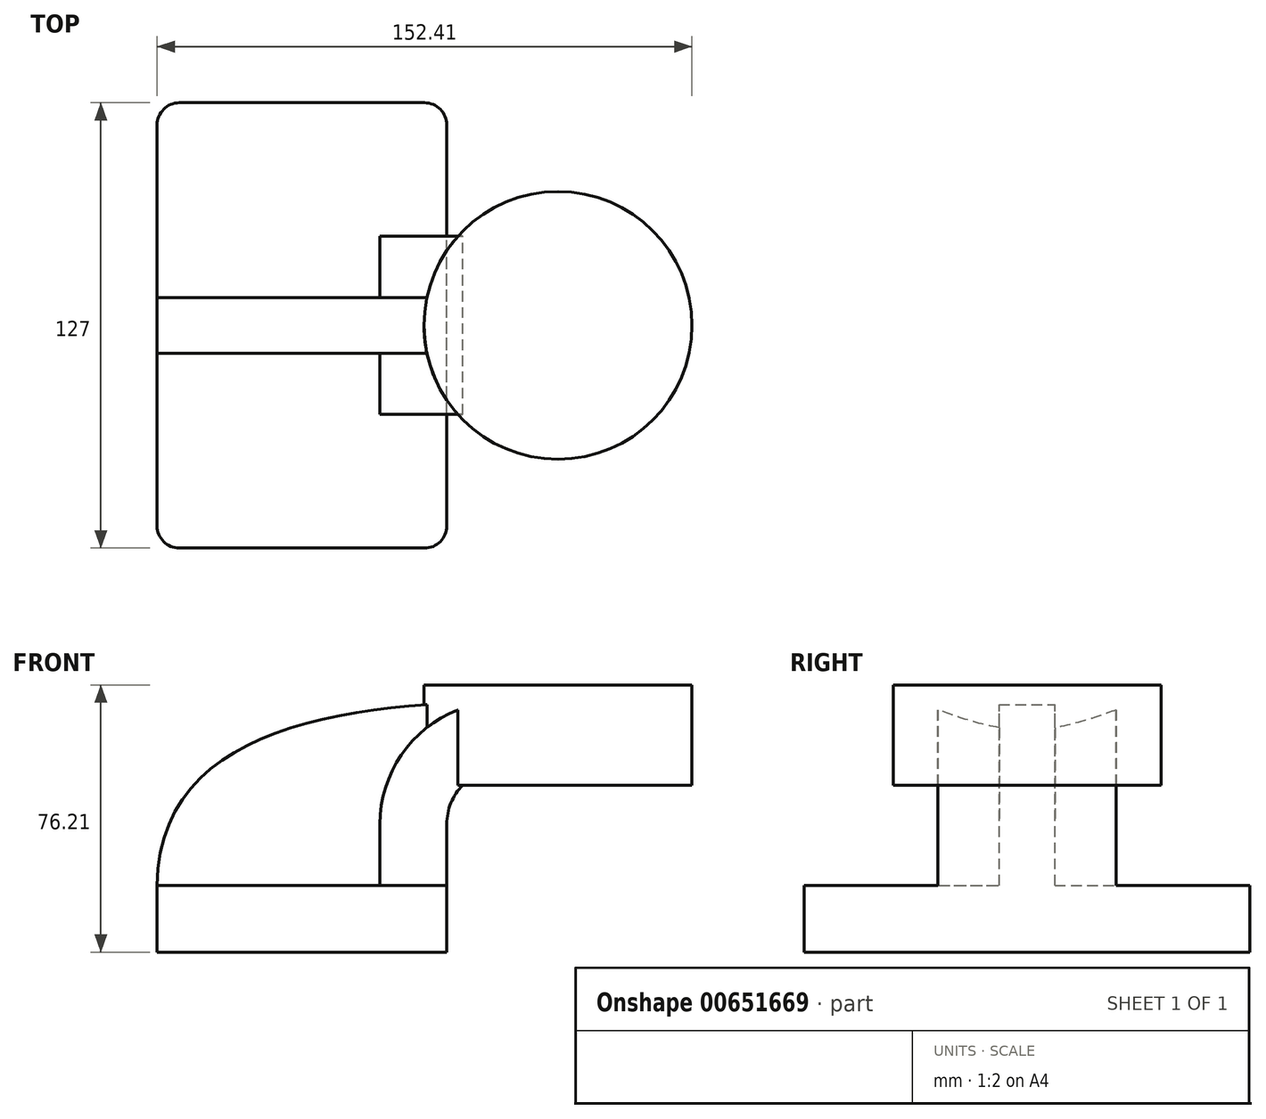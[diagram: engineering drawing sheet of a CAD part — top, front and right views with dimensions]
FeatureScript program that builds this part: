
annotation { "Feature Type Name" : "Feature", "Feature Type Description" : "" }
export const myFeature = defineFeature(function(context is Context, id is Id, definition is map)
    precondition{}
    {
        {
            var Q0;
            Q0=qCreatedBy(makeId("Front.planeOp"),FACE);
            var sketch = newSketch(context, id + "F0", { "sketchPlane" : qUnion([Q0])});
            skLineSegment(sketch, "E0.bottom", {"start": v(-41.28, 9.52) * mm, "end": v(41.27, 9.53) * mm});
            skLineSegment(sketch, "E0.top", {"start": v(-41.28, -9.52) * mm, "end": v(41.28, -9.52) * mm});
            skLineSegment(sketch, "E0.left", {"start": v(-41.28, 9.52) * mm, "end": v(-41.28, -9.53) * mm});
            skLineSegment(sketch, "E0.right", {"start": v(41.27, 9.53) * mm, "end": v(41.28, -9.52) * mm});
            skPoint(sketch, "E0.middle", {"position": v(0, 0) * mm});
            skLineSegment(sketch, "E1.bottom", {"start": v(111.12, 38.1) * mm, "end": v(60.32, 38.1) * mm});
            skLineSegment(sketch, "E1.top", {"start": v(111.12, 66.68) * mm, "end": v(60.32, 66.68) * mm});
            skLineSegment(sketch, "E1.left", {"start": v(111.12, 38.1) * mm, "end": v(111.12, 66.68) * mm});
            skLineSegment(sketch, "E1.right", {"start": v(60.32, 38.1) * mm, "end": v(60.32, 66.68) * mm});
            skPoint(sketch, "E1.middle", {"position": v(85.72, 52.39) * mm});
            skLineSegment(sketch, "E2", {"start": v(41.27, 9.53) * mm, "end": v(41.27, 27) * mm});
            skArc(sketch, "E3", {"start": v(41.27, 27) * mm, "mid": v(45.92, 38.23) * mm, "end": v(57.15, 42.88) * mm});
            skLineSegment(sketch, "E4", {"start": v(57.15, 42.88) * mm, "end": v(72.95, 42.88) * mm});
            skLineSegment(sketch, "E5.0", {"start": v(57.15, 61.93) * mm, "end": v(72.95, 61.93) * mm});
            skArc(sketch, "E5.1", {"start": v(22.22, 27) * mm, "mid": v(32.45, 51.7) * mm, "end": v(57.15, 61.93) * mm});
            skLineSegment(sketch, "E5.2", {"start": v(22.22, 9.53) * mm, "end": v(22.22, 27) * mm});
            skLineSegment(sketch, "E6", {"start": v(72.95, 42.88) * mm, "end": v(72.95, 66.68) * mm});
            skLineSegment(sketch, "E7", {"start": v(72.95, 66.68) * mm, "end": v(72.95, 38.1) * mm});
            skFitSpline(sketch, "E8", {"points": [v(-41.28, 9.52) * mm, v(57.15, 61.93) * mm], "startDerivative": vector(1.24, 134.3) * mm, "endDerivative": vector(138.83, 2.17) * mm});
            skSolve(sketch);
        }
        {
            var Q0;
            Q0=makeQuery(id+"F0.imprint","IMPRINT",FACE,{"disambiguationData":[TD([[makeQuery(id+"F0.imprint","IMPRINT",EDGE,{"derivedFrom":sQuery(id+"F0.wireOp",EDGE,"E0.top")}),1.0]])]});
            extrude(context, id + "F1", {"entities" : qUnion([Q0]), "endBound" : BoundingType.SYMMETRIC, "depth" : 127 * mm, "offsetDistance" : 25.4 * mm});
        }
        {
            var Q0;
            {var subQ1=sQuery(id+"F0.wireOp",EDGE,"E2");Q0=makeQuery(id+"F0.imprint","IMPRINT",FACE,{"disambiguationData":[TD([[makeQuery(id+"F0.imprint","IMPRINT",EDGE,{"derivedFrom":subQ1}),1.0]])]});}
            var Q1;
            {var subQ0=sQuery(id+"F0.wireOp",EDGE,"E4");var subQ1=sQuery(id+"F0.wireOp",EDGE,"E1.right");var subQ2=makeQuery(id+"F0.imprint","INTERSECT",VERTEX,{"derivedFrom":[subQ1,subQ0]});Q1=makeQuery(id+"F0.imprint","IMPRINT",FACE,{"disambiguationData":[TD([[makeQuery(id+"F0.imprint","IMPRINT",EDGE,{"disambiguationData":[TD([[subQ2,-1.0]])],"derivedFrom":subQ1}),-1.0]])]});}
            extrude(context, id + "F2", {"entities" : qUnion([Q0, Q1]), "operationType" : NewBodyOperationType.ADD, "endBound" : BoundingType.SYMMETRIC, "depth" : 50.8 * mm, "offsetDistance" : 25.4 * mm});
        }
        {
            var Q0;
            {var subQ3=sQuery(id+"F0.wireOp",EDGE,"E5.2");Q0=makeQuery(id+"F0.imprint","IMPRINT",FACE,{"disambiguationData":[TD([[makeQuery(id+"F0.imprint","IMPRINT",EDGE,{"derivedFrom":subQ3}),1.0]])]});}
            extrude(context, id + "F3", {"entities" : qUnion([Q0]), "operationType" : NewBodyOperationType.ADD, "endBound" : BoundingType.SYMMETRIC, "depth" : 15.88 * mm, "offsetDistance" : 25.4 * mm});
        }
        {
            var Q0;
            {var subQ0=sQuery(id+"F0.wireOp",EDGE,"E1.left");Q0=makeQuery(id+"F0.imprint","IMPRINT",FACE,{"disambiguationData":[TD([[makeQuery(id+"F0.imprint","IMPRINT",EDGE,{"derivedFrom":subQ0}),1.0]])]});}
            var Q1;
            Q1=sQuery(id+"F0.wireOp",EDGE,"E7");
            revolve(context, id + "F4", {"operationType" : NewBodyOperationType.ADD, "entities" : qUnion([Q0]), "axis" : qUnion([Q1]), "revolveType" : RevolveType.FULL});
        }
        {
            var Q0;
            Q0=makeQuery(id+"F1.opExtrude","CAP_EDGE",EDGE,{"disambiguationData":[OSD([sQuery(id+"F0.wireOp",EDGE,"E0.right")])],"isStart":false});
            var Q1;
            Q1=makeQuery(id+"F1.opExtrude","CAP_EDGE",EDGE,{"disambiguationData":[OSD([sQuery(id+"F0.wireOp",EDGE,"E0.left")])],"isStart":false});
            var Q2;
            Q2=makeQuery(id+"F1.opExtrude","CAP_EDGE",EDGE,{"disambiguationData":[OSD([sQuery(id+"F0.wireOp",EDGE,"E0.right")])],"isStart":true});
            var Q3;
            Q3=makeQuery(id+"F1.opExtrude","CAP_EDGE",EDGE,{"disambiguationData":[OSD([sQuery(id+"F0.wireOp",EDGE,"E0.left")])],"isStart":true});
            fillet(context, id + "F5", {"entities" : qUnion([Q0, Q1, Q2, Q3]), "radius" : 6.35 * mm, "tangentPropagation" : true, "allowEdgeOverflow" : false});
        }
    });
